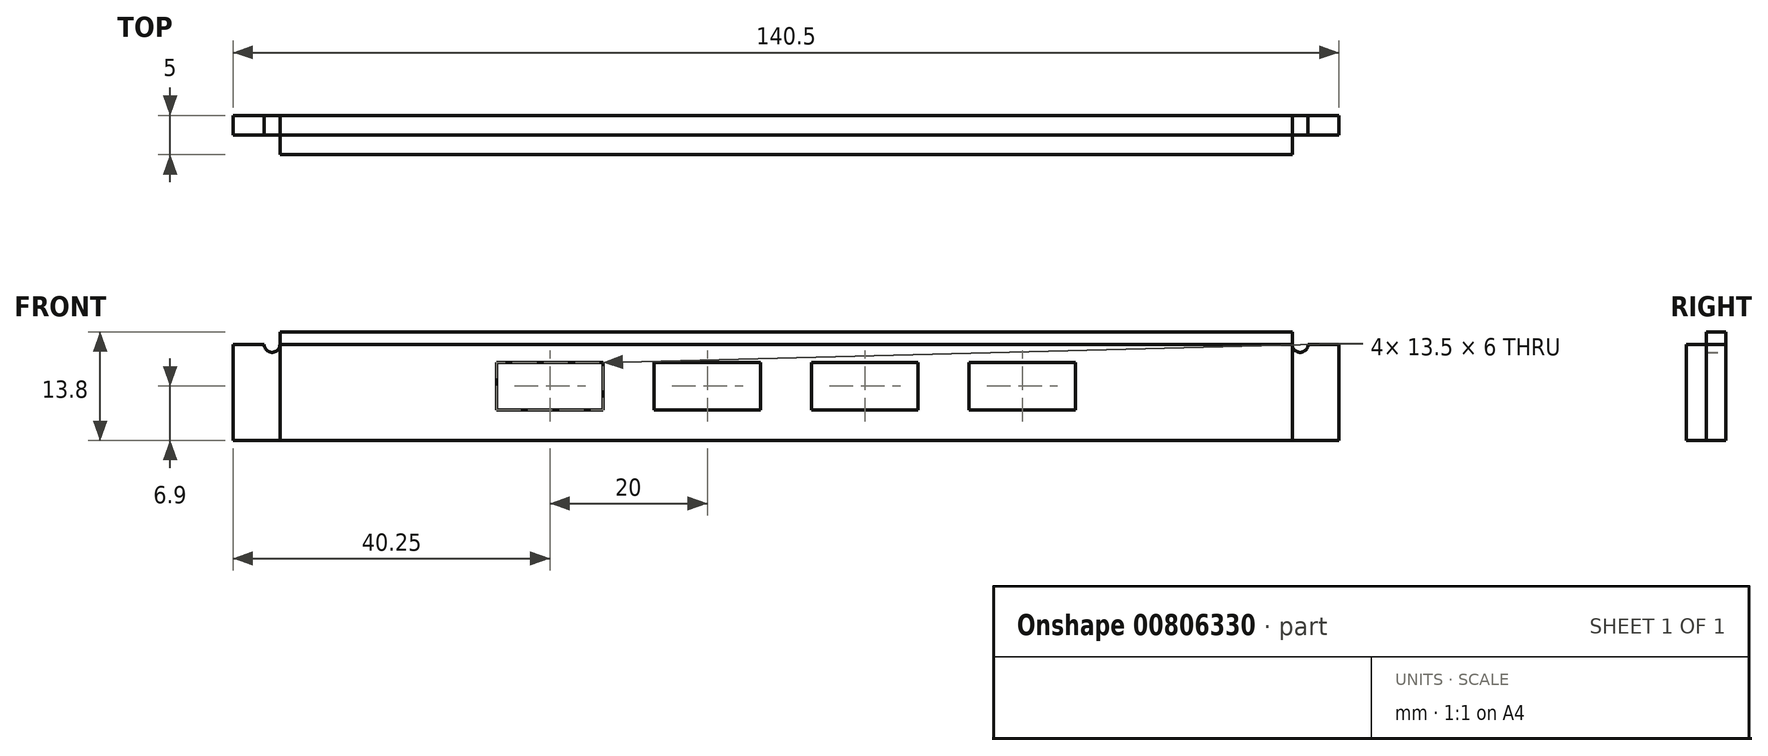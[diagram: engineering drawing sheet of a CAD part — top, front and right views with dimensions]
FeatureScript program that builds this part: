
annotation { "Feature Type Name" : "Feature", "Feature Type Description" : "" }
export const myFeature = defineFeature(function(context is Context, id is Id, definition is map)
    precondition{}
    {
        {
            var Q0;
            Q0=qCreatedBy(makeId("Front.planeOp"),FACE);
            var sketch = newSketch(context, id + "F0", { "sketchPlane" : qUnion([Q0])});
            skLineSegment(sketch, "E0.bottom", {"start": v(64.3, 6.9) * mm, "end": v(-64.3, 6.9) * mm});
            skLineSegment(sketch, "E0.top", {"start": v(64.3, -6.9) * mm, "end": v(-64.3, -6.9) * mm});
            skLineSegment(sketch, "E0.left", {"start": v(64.3, 6.9) * mm, "end": v(64.3, -6.9) * mm});
            skLineSegment(sketch, "E0.right", {"start": v(-64.3, 6.9) * mm, "end": v(-64.3, -6.9) * mm});
            skPoint(sketch, "E0.middle", {"position": v(0, 0) * mm});
            skLineSegment(sketch, "E1", {"start": v(-64.3, -6.9) * mm, "end": v(-70.25, -6.9) * mm, "construction": true});
            skLineSegment(sketch, "E2", {"start": v(64.3, -6.9) * mm, "end": v(70.25, -6.9) * mm, "construction": true});
            skLineSegment(sketch, "E3.bottom", {"start": v(-70.25, -6.9) * mm, "end": v(70.25, -6.9) * mm});
            skLineSegment(sketch, "E3.top", {"start": v(-70.25, 5.3) * mm, "end": v(70.25, 5.3) * mm});
            skLineSegment(sketch, "E3.left", {"start": v(-70.25, -6.9) * mm, "end": v(-70.25, 5.3) * mm});
            skLineSegment(sketch, "E3.right", {"start": v(70.25, -6.9) * mm, "end": v(70.25, 5.3) * mm});
            skCircle(sketch, "E4", {"center": v(65.3, 5.3) * mm, "radius": 1 * mm});
            skCircle(sketch, "E5", {"center": v(-65.3, 5.3) * mm, "radius": 1 * mm});
            skLineSegment(sketch, "E6", {"start": v(-64.3, 0) * mm, "end": v(64.3, 0) * mm, "construction": true});
            skLineSegment(sketch, "E7.bottom", {"start": v(-23.25, 3) * mm, "end": v(-36.75, 3) * mm});
            skLineSegment(sketch, "E7.top", {"start": v(-23.25, -3) * mm, "end": v(-36.75, -3) * mm});
            skLineSegment(sketch, "E7.left", {"start": v(-23.25, 3) * mm, "end": v(-23.25, -3) * mm});
            skLineSegment(sketch, "E7.right", {"start": v(-36.75, 3) * mm, "end": v(-36.75, -3) * mm});
            skPoint(sketch, "E7.middle", {"position": v(-30, 0) * mm});
            skLineSegment(sketch, "E8.bottom", {"start": v(-3.25, 3) * mm, "end": v(-16.75, 3) * mm});
            skLineSegment(sketch, "E8.top", {"start": v(-3.25, -3) * mm, "end": v(-16.75, -3) * mm});
            skLineSegment(sketch, "E8.left", {"start": v(-3.25, 3) * mm, "end": v(-3.25, -3) * mm});
            skLineSegment(sketch, "E8.right", {"start": v(-16.75, 3) * mm, "end": v(-16.75, -3) * mm});
            skPoint(sketch, "E8.middle", {"position": v(-10, 0) * mm});
            skLineSegment(sketch, "E9.bottom", {"start": v(16.75, 3) * mm, "end": v(3.25, 3) * mm});
            skLineSegment(sketch, "E9.top", {"start": v(16.75, -3) * mm, "end": v(3.25, -3) * mm});
            skLineSegment(sketch, "E9.left", {"start": v(16.75, 3) * mm, "end": v(16.75, -3) * mm});
            skLineSegment(sketch, "E9.right", {"start": v(3.25, 3) * mm, "end": v(3.25, -3) * mm});
            skPoint(sketch, "E9.middle", {"position": v(10, 0) * mm});
            skLineSegment(sketch, "E10.bottom", {"start": v(36.75, 3) * mm, "end": v(23.25, 3) * mm});
            skLineSegment(sketch, "E10.top", {"start": v(36.75, -3) * mm, "end": v(23.25, -3) * mm});
            skLineSegment(sketch, "E10.left", {"start": v(36.75, 3) * mm, "end": v(36.75, -3) * mm});
            skLineSegment(sketch, "E10.right", {"start": v(23.25, 3) * mm, "end": v(23.25, -3) * mm});
            skPoint(sketch, "E10.middle", {"position": v(30, 0) * mm});
            skPoint(sketch, "E11", {"position": v(-36.75, 0) * mm});
            skPoint(sketch, "E12", {"position": v(36.75, 0) * mm});
            skSolve(sketch);
        }
        {
            var Q0;
            Q0=makeQuery(id+"F0.imprint","IMPRINT",FACE,{"disambiguationData":[TD([[makeQuery(id+"F0.imprint","IMPRINT",EDGE,{"derivedFrom":sQuery(id+"F0.wireOp",EDGE,"E7.bottom")}),-1.0]])]});
            extrude(context, id + "F1", {"entities" : qUnion([Q0]), "depth" : 5 * mm, "offsetDistance" : 25 * mm});
        }
        {
            var Q0;
            {var subQ0=sQuery(id+"F0.wireOp",EDGE,"E3.left");Q0=makeQuery(id+"F0.imprint","IMPRINT",FACE,{"disambiguationData":[TD([[makeQuery(id+"F0.imprint","IMPRINT",EDGE,{"derivedFrom":subQ0}),-1.0]])]});}
            var Q1;
            {var subQ0=sQuery(id+"F0.wireOp",EDGE,"E0.bottom");Q1=makeQuery(id+"F0.imprint","IMPRINT",FACE,{"disambiguationData":[TD([[makeQuery(id+"F0.imprint","IMPRINT",EDGE,{"derivedFrom":subQ0}),1.0]])]});}
            var Q2;
            {var subQ0=sQuery(id+"F0.wireOp",EDGE,"E3.right");Q2=makeQuery(id+"F0.imprint","IMPRINT",FACE,{"disambiguationData":[TD([[makeQuery(id+"F0.imprint","IMPRINT",EDGE,{"derivedFrom":subQ0}),1.0]])]});}
            extrude(context, id + "F2", {"entities" : qUnion([Q0, Q1, Q2]), "operationType" : NewBodyOperationType.ADD, "depth" : 2.5 * mm, "offsetDistance" : 25 * mm});
        }
    });
